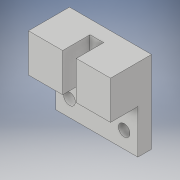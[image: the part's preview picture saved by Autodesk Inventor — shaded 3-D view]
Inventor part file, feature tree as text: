
AUTODESK INVENTOR PART (.ipt)
format: ipt  version: 2019 (Build 230136000, 136)  size: 251,392 bytes
history: native  units: in
note: dims shown in document units (in); Inventor stores cm internally (conversion verified against a paired STEP export)
features: extrude x2, sketch x2
ambient origin geometry x8: Origin, YZ Plane, XZ Plane, XY Plane, X Axis, Y Axis, Z Axis, Center Point
bodies: Solid1 (feature_tree)
feature tree (4):
  extrude  "Extrusion1"  Depth=1.1811in
  extrude  "Extrusion2"  Depth=0.1969in
  sketch  "Sketch1"  dims[d2=1.1811in d3=1.1811in]
  sketch  "Sketch2"  dims[d4=0.1969in d5=0.0in d6=0.1969in d7=0.5512in d8=0.3937in d9=0.0in d10=0.1673in d11=0.1673in d12=0.1969in d13=0.2362in]
